FCSTD DOCUMENT  (FreeCAD 0.20R29410 (Git))
Label: SNO+Mockup
License: All rights reserved
LicenseURL: http://en.wikipedia.org/wiki/All_rights_reserved
objects: Part::FeaturePython×3, Part::Sphere×2, Part::Cut×2, Part::Cylinder×2, Part::Fuse×1, Part::MultiFuse×1
note: 11 computed .brp shape members not serialized (recipe doc carries the construction recipe); baked Part::Feature solids carry a one-line shape summary decoded from their .brp

FEATURE [Part::Sphere] Sphere
  Angle1 = -90
  Angle2 = 90
  Angle3 = 360
  AttacherType = Attacher::AttachEngine3D
  Radius = 6000
FEATURE [Part::Sphere] Sphere001
  Angle1 = -90
  Angle2 = 90
  Angle3 = 360
  AttacherType = Attacher::AttachEngine3D
  Radius = 6060
FEATURE [Part::Cut] Cut
  Base = -> Sphere001
  Tool = -> Sphere
FEATURE [Part::FeaturePython] Tube  # WARN: FeaturePython — macro-defined, semantics opaque (R4)
  AttacherType = Attacher::AttachEngine3D
  Height = 7000
  InnerRadius = 649
  OuterRadius = 710
  Placement = pos=(0,0,6000) rot=(0,0,1;0rad)
FEATURE [Part::Cylinder] Cylinder
  Angle = 360
  AttacherType = Attacher::AttachEngine3D
  FirstAngle = 0
  Height = 1000
  Placement = pos=(0,0,5950) rot=(0,0,1;0rad)
  Radius = 590
  SecondAngle = 0
FEATURE [Part::Cut] Cut001
  Base = -> Cut
  Tool = -> Cylinder
FEATURE [Part::Fuse] Fusion
  Base = -> Cut001
  Tool = -> Tube
FEATURE [Part::FeaturePython] Tube001  # WARN: FeaturePython — macro-defined, semantics opaque (R4)
  AttacherType = Attacher::AttachEngine3D
  Height = 500
  InnerRadius = 649
  OuterRadius = 655
  Placement = pos=(0,0,13000) rot=(0,0,1;0rad)
FEATURE [Part::FeaturePython] Tube002  # WARN: FeaturePython — macro-defined, semantics opaque (R4)
  AttacherType = Attacher::AttachEngine3D
  Height = 500
  InnerRadius = 649
  OuterRadius = 655
  Placement = pos=(0,0,13500) rot=(0,0,1;0rad)
FEATURE [Part::Cylinder] Cylinder001
  Angle = 360
  AttacherType = Attacher::AttachEngine3D
  FirstAngle = 0
  Height = 13
  Placement = pos=(0,0,14000) rot=(0,0,1;0rad)
  Radius = 655
  SecondAngle = 0
FEATURE [Part::MultiFuse] Fusion001
  Shapes = -> [Tube002,Cylinder001]
